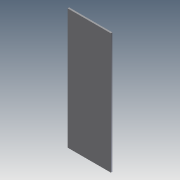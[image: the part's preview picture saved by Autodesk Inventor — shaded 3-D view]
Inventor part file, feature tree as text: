
AUTODESK INVENTOR PART (.ipt)
format: ipt  version: 2011 (Build 150239000, 239)  size: 65,536 bytes
history: native  units: in
note: dims shown in document units (in); Inventor stores cm internally (conversion verified against a paired STEP export)
features: extrude x1, sketch x1
ambient origin geometry x8: Origin, YZ Plane, XZ Plane, XY Plane, X Axis, Y Axis, Z Axis, Center Point
bodies: Solid1 (feature_tree)
feature tree (2):
  extrude  "Extrusion1"  Depth=18.97in
  sketch  "Sketch1"  dims[d0=6.81in d1=18.97in d2=0.25in d3=0.0in]
